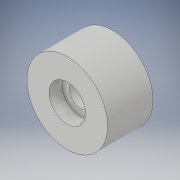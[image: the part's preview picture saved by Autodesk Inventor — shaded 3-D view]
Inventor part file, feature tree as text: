
AUTODESK INVENTOR PART (.ipt)
format: ipt  version: 2018.2 (Build 222227000, 227)  size: 108,032 bytes
history: native  units: in
note: dims shown in document units (in); Inventor stores cm internally (conversion verified against a paired STEP export)
features: extrude x3, sketch x3
ambient origin geometry x8: Origin, YZ Plane, XZ Plane, XY Plane, X Axis, Y Axis, Z Axis, Center Point
bodies: Solid1 (feature_tree)
feature tree (6):
  extrude  "Extrusion1"  Depth=0.3524in TaperAngle=0.0deg
  extrude  "Extrusion2"  Depth=0.1024in TaperAngle=0.0deg
  extrude  "Extrusion3"  Depth=0.2899in TaperAngle=0.0deg
  sketch  "Sketch1"  dims[d0=0.626in d1=0.3524in d2=0.0in]
  sketch  "Sketch2"  dims[d3=0.2835in d4=0.1024in d5=0.0in]
  sketch  "Sketch3"  dims[d6=0.1732in d7=0.2899in d8=0.0in]
